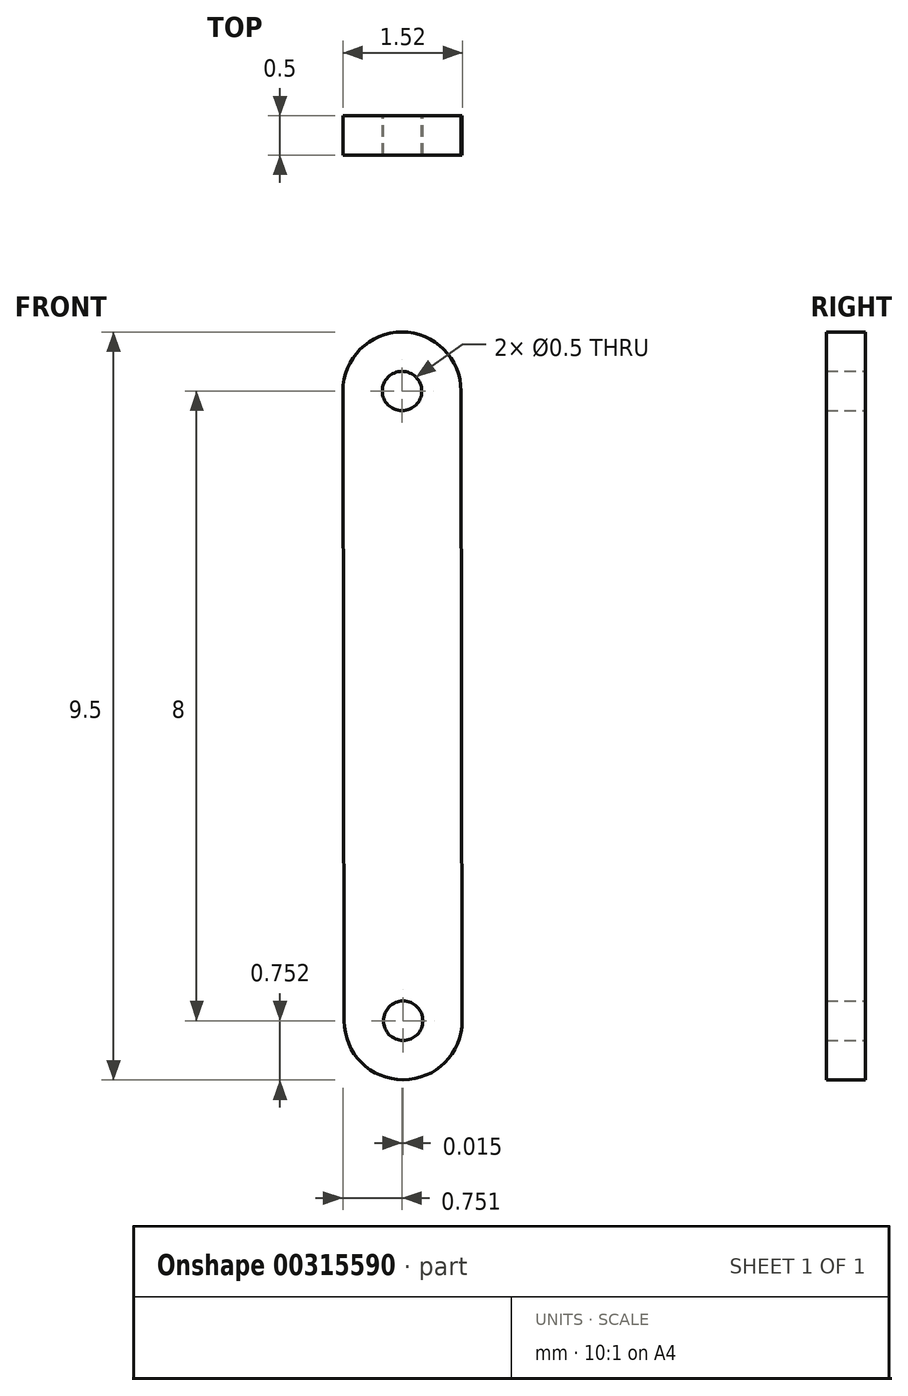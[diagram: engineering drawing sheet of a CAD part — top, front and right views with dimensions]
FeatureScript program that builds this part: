
annotation { "Feature Type Name" : "Feature", "Feature Type Description" : "" }
export const myFeature = defineFeature(function(context is Context, id is Id, definition is map)
    precondition{}
    {
        {
            var Q0;
            Q0=qCreatedBy(makeId("Front.planeOp"),FACE);
            var sketch = newSketch(context, id + "F0", { "sketchPlane" : qUnion([Q0])});
            skCircle(sketch, "E0", {"center": v(-1.02, 13.51) * mm, "radius": 0.25 * mm});
            skCircle(sketch, "E1", {"center": v(-1, 5.51) * mm, "radius": 0.25 * mm});
            skArc(sketch, "E2", {"start": v(-1.75, 5.51) * mm, "mid": v(-1, 4.76) * mm, "end": v(-0.25, 5.51) * mm});
            skArc(sketch, "E3", {"start": v(-0.27, 13.51) * mm, "mid": v(-1.02, 14.26) * mm, "end": v(-1.77, 13.51) * mm});
            skLineSegment(sketch, "E4", {"start": v(-1.77, 13.51) * mm, "end": v(-1.75, 5.51) * mm});
            skLineSegment(sketch, "E5", {"start": v(-0.27, 13.51) * mm, "end": v(-0.25, 5.51) * mm});
            skSolve(sketch);
        }
        {
            var Q0;
            Q0 = qSketchRegion(id + "F0", true);
            extrude(context, id + "F1", {"entities" : qUnion([Q0]), "depth" : .5 * mm});
        }
    });
